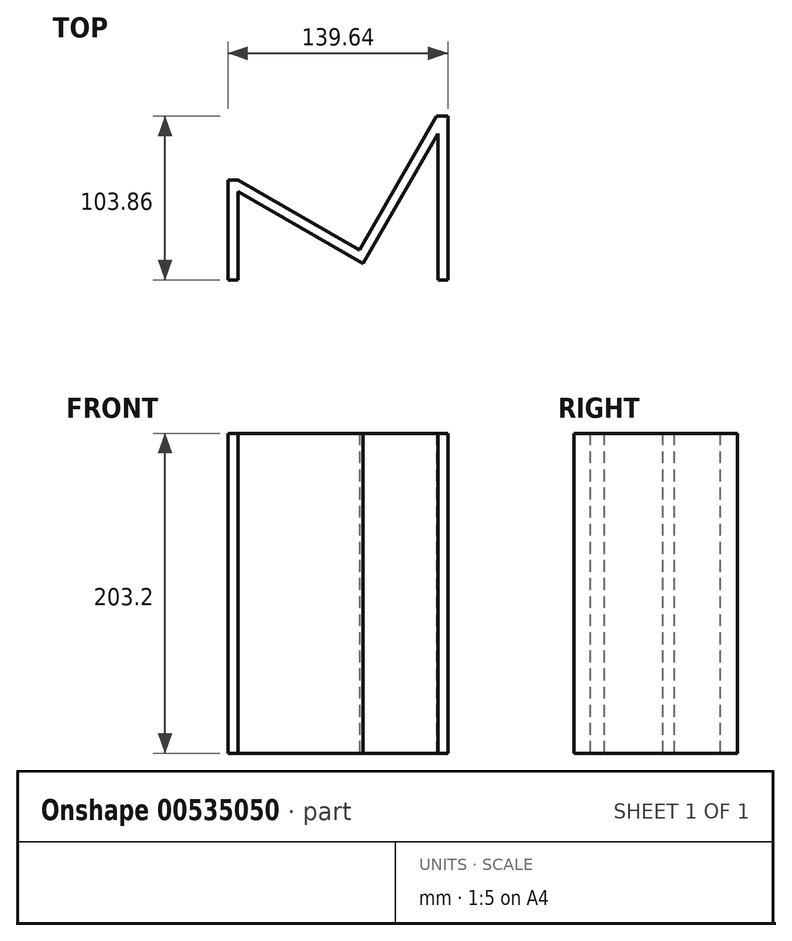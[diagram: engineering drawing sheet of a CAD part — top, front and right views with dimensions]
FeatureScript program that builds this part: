
annotation { "Feature Type Name" : "Feature", "Feature Type Description" : "" }
export const myFeature = defineFeature(function(context is Context, id is Id, definition is map)
    precondition{}
    {
        {
            var Q0;
            Q0=qCreatedBy(makeId("Top.planeOp"),FACE);
            var sketch = newSketch(context, id + "F0", { "sketchPlane" : qUnion([Q0])});
            skLineSegment(sketch, "E0", {"start": v(97.68, 0) * mm, "end": v(-97.93, 0) * mm, "construction": true});
            skLineSegment(sketch, "E1.bottom", {"start": v(-97.93, 0) * mm, "end": v(-91.58, 0) * mm});
            skLineSegment(sketch, "E1.top", {"start": v(-97.93, 63.5) * mm, "end": v(-91.58, 63.5) * mm});
            skLineSegment(sketch, "E1.left", {"start": v(-97.93, 0) * mm, "end": v(-97.93, 63.5) * mm});
            skLineSegment(sketch, "E1.right", {"start": v(-91.58, 0) * mm, "end": v(-91.58, 63.5) * mm});
            skLineSegment(sketch, "E2", {"start": v(-91.58, 63.5) * mm, "end": v(-14.59, 19.05) * mm});
            skLineSegment(sketch, "E3", {"start": v(-14.59, -53.67) * mm, "end": v(-14.59, 127.05) * mm, "construction": true});
            skLineSegment(sketch, "E4", {"start": v(-91.58, 56.17) * mm, "end": v(-12.26, 10.38) * mm});
            skLineSegment(sketch, "E5", {"start": v(41.71, 103.86) * mm, "end": v(41.71, 0) * mm});
            skLineSegment(sketch, "E6", {"start": v(35.36, 92.86) * mm, "end": v(35.36, 0) * mm});
            skLineSegment(sketch, "E7", {"start": v(35.36, 0) * mm, "end": v(41.71, 0) * mm});
            skLineSegment(sketch, "E8", {"start": v(-12.26, 10.38) * mm, "end": v(35.36, 92.86) * mm});
            skLineSegment(sketch, "E9", {"start": v(41.71, 103.86) * mm, "end": v(-44.41, 103.86) * mm, "construction": true});
            skLineSegment(sketch, "E10", {"start": v(-14.59, 19.05) * mm, "end": v(34.38, 103.86) * mm});
            skLineSegment(sketch, "E11", {"start": v(34.38, 103.86) * mm, "end": v(41.71, 103.86) * mm});
            skSolve(sketch);
        }
        {
            var Q0;
            Q0 = qSketchRegion(id + "F0", true);
            extrude(context, id + "F1", {"entities" : qUnion([Q0]), "depth" : 203.2 * mm, "offsetDistance" : 25.4 * mm});
        }
    });
